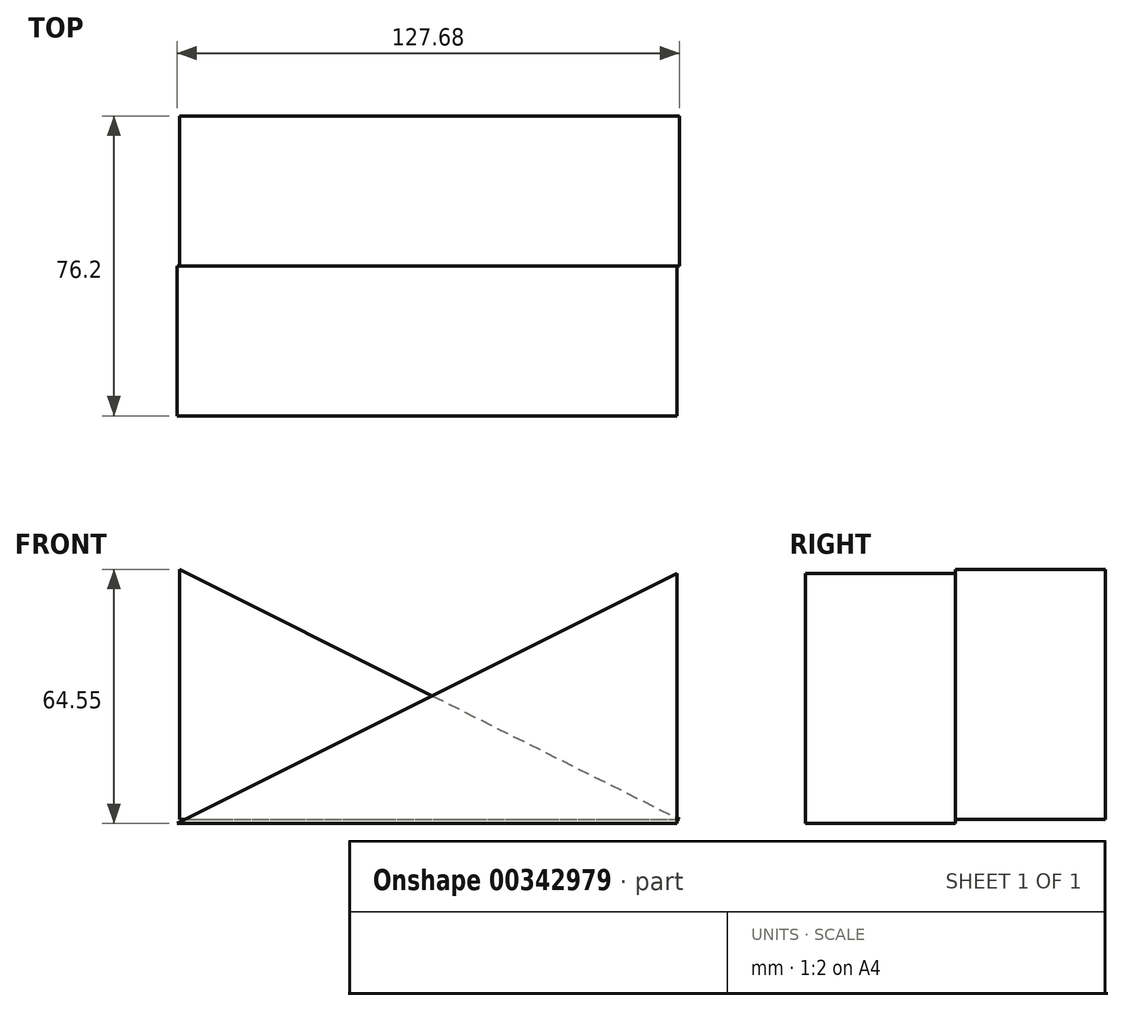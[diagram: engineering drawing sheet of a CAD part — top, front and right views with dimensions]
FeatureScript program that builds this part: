
annotation { "Feature Type Name" : "Feature", "Feature Type Description" : "" }
export const myFeature = defineFeature(function(context is Context, id is Id, definition is map)
    precondition{}
    {
        {
            var Q0;
            Q0=qCreatedBy(makeId("Front.planeOp"),FACE);
            var sketch = newSketch(context, id + "F0", { "sketchPlane" : qUnion([Q0])});
            skLineSegment(sketch, "E0", {"start": v(-68.06, -31.63) * mm, "end": v(58.94, -31.63) * mm});
            skLineSegment(sketch, "E1", {"start": v(58.94, -31.63) * mm, "end": v(58.94, 31.87) * mm});
            skLineSegment(sketch, "E2", {"start": v(-68.06, -31.63) * mm, "end": v(58.94, 31.87) * mm});
            skSolve(sketch);
        }
        {
            var Q0;
            Q0=makeQuery(id+"F0.imprint","IMPRINT",FACE,{"disambiguationData":[TD([[makeQuery(id+"F0.imprint","IMPRINT",EDGE,{"derivedFrom":sQuery(id+"F0.wireOp",EDGE,"E0")}),1.0]])]});
            extrude(context, id + "F1", {"entities" : qUnion([Q0]), "depth" : 38.1 * mm});
        }
        {
            var Q0;
            Q0=qCreatedBy(makeId("Front.planeOp"),FACE);
            var sketch = newSketch(context, id + "F2", { "sketchPlane" : qUnion([Q0])});
            skLineSegment(sketch, "E3", {"start": v(-67.38, -30.58) * mm, "end": v(-67.38, 32.92) * mm});
            skLineSegment(sketch, "E4", {"start": v(-67.38, -30.58) * mm, "end": v(59.62, -30.58) * mm});
            skLineSegment(sketch, "E5", {"start": v(-67.38, 32.92) * mm, "end": v(59.62, -30.58) * mm});
            skSolve(sketch);
        }
        {
            var Q0;
            Q0=makeQuery(id+"F2.imprint","IMPRINT",FACE,{"disambiguationData":[TD([[makeQuery(id+"F2.imprint","IMPRINT",EDGE,{"derivedFrom":sQuery(id+"F2.wireOp",EDGE,"E3")}),-1.0]])]});
            extrude(context, id + "F3", {"entities" : qUnion([Q0]), "operationType" : NewBodyOperationType.ADD, "oppositeDirection" : true, "depth" : 38.1 * mm});
        }
    });
